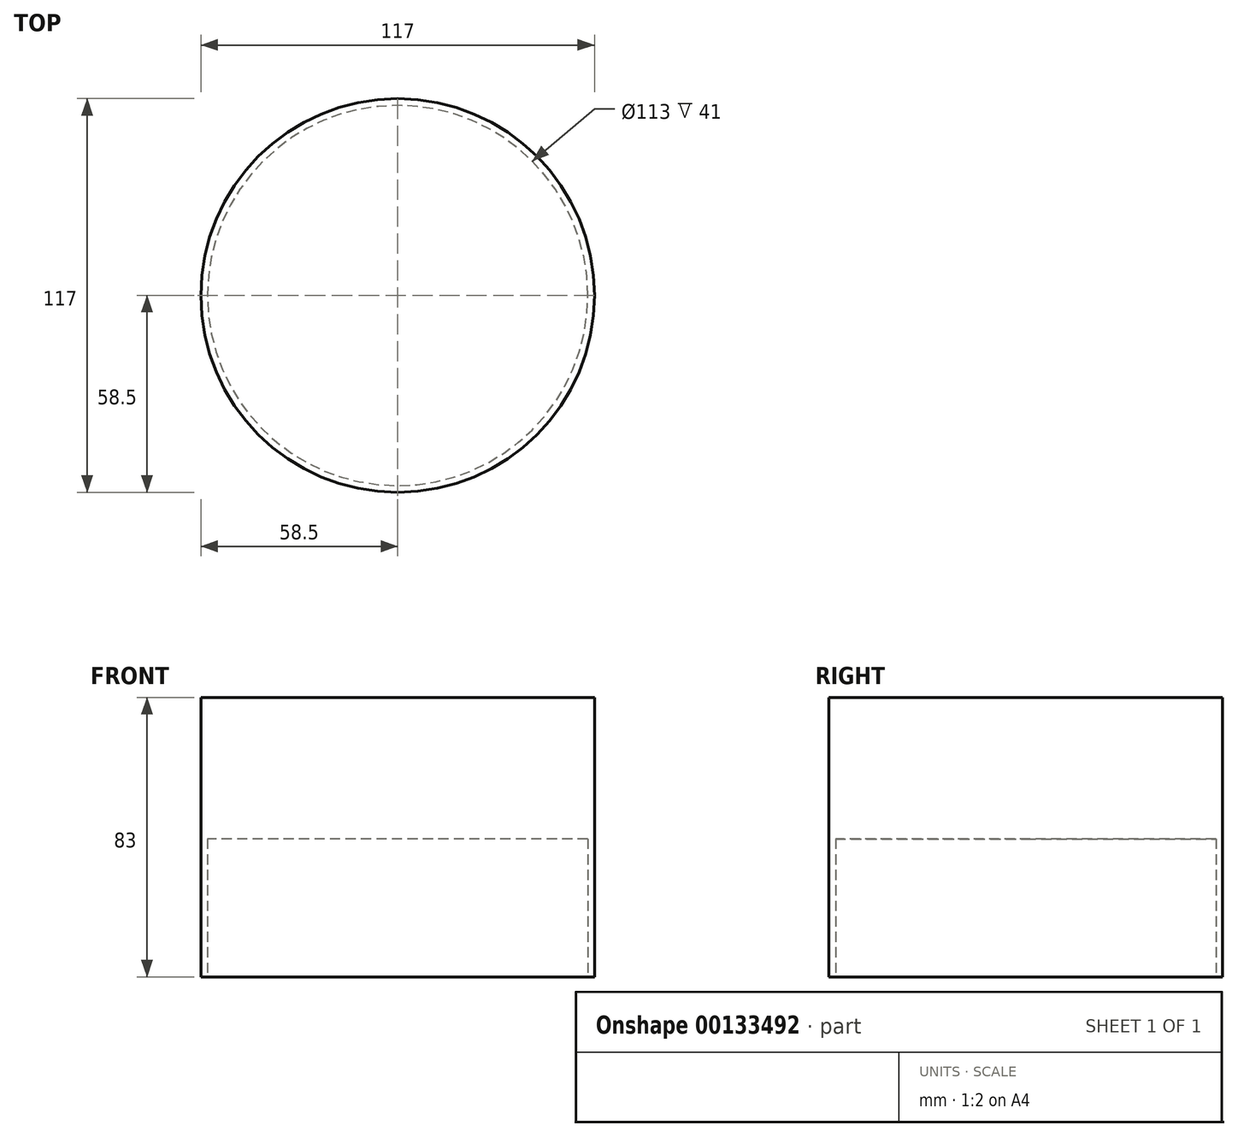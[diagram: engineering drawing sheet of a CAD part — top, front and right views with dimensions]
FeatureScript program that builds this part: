
annotation { "Feature Type Name" : "Feature", "Feature Type Description" : "" }
export const myFeature = defineFeature(function(context is Context, id is Id, definition is map)
    precondition{}
    {
        {
            var Q0;
            Q0=qCreatedBy(makeId("Top.planeOp"),FACE);
            var sketch = newSketch(context, id + "F0", { "sketchPlane" : qUnion([Q0])});
            skCircle(sketch, "E0", {"center": v(0, 0) * mm, "radius": 58.5 * mm});
            skSolve(sketch);
        }
        {
            var Q0;
            Q0=makeQuery(id+"F0.imprint","IMPRINT",FACE,{"disambiguationData":[TD([[makeQuery(id+"F0.imprint","IMPRINT",EDGE,{"derivedFrom":sQuery(id+"F0.wireOp",EDGE,"E0")}),1.0]])]});
            extrude(context, id + "F1", {"entities" : qUnion([Q0]), "depth" : 83 * mm});
        }
        {
            var Q0;
            Q0=qCreatedBy(makeId("Top.planeOp"),FACE);
            var sketch = newSketch(context, id + "F2", { "sketchPlane" : qUnion([Q0])});
            skCircle(sketch, "E1", {"center": v(0, 0) * mm, "radius": 56.5 * mm});
            skSolve(sketch);
        }
        {
            var Q0;
            Q0 = qSketchRegion(id + "F2", true);
            extrude(context, id + "F3", {"entities" : qUnion([Q0]), "operationType" : NewBodyOperationType.REMOVE, "depth" : 41 * mm});
        }
        {
            var Q0;
            Q0=makeQuery(id+"F3.boolean.opBoolean","COPY",FACE,{"derivedFrom":makeQuery(id+"F3.opExtrude","CAP_FACE",FACE,{"disambiguationData":[OSD([sQuery(id+"F2.wireOp",EDGE,"E1")])],"isStart":false})});
            var sketch = newSketch(context, id + "F4", { "sketchPlane" : qUnion([Q0])});
            skCircle(sketch, "E2", {"center": v(0, 0) * mm, "radius": 43 * mm});
            skLineSegment(sketch, "E3", {"start": v(0, 0) * mm, "end": v(-43, 0) * mm, "construction": true});
            skSolve(sketch);
        }
    });
